# Revit family: Gira_239902
name_source: partatom
category: Electrical Fixtures
revit_build: Autodesk Revit 2017 (Build: 20160225_1515(x64)
units: mm (PartAtom-declared; Revit-internal decimal feet)

## family parameters
Cut with Voids When Loaded = No
Host = Face
Maintain Annotation Orientation = Yes
Part Type = Normal
Room Calculation Point = No
Round Connector Dimension = Use Diameter
Shared = No

## types (1)
- Pres. + motion detec. 360° Kompakt Sentinel
    Available = No
    BIM (1) = https://media.stage.bim.site
    Category = Accessories for movement sensor
    Data sheet (1) = https://katalog.gira.de
    Default Elevation = 1219 mm
    Description = Pres. mot.det.360° Kompakt Sent,Presence detector and motion detector 360 compact,,,Features:,- Automatic switching of lighting, depending on the movement of heat and ambient brightness.,- 2-point light control.,- Functions can be adjusted with IR remote controls.,- Restricting the detection field by switching off individual sensors or clip-on panel.,- Operation with IR remote control, auxiliary unit 2-wire or rocker button.,- Teach-in function for adapting the brightness threshold, in combination with IR remote controls.,- Switch-off pre-warning.,- Short-term operation, e.g. for controlling acoustic signal transmitters.,- Occupied-home simulation.,- Function as twilight switch.,- Dynamic delay time.,- Extension of the detection field by connecting several devices in parallel.,,Notes :,- The required settings for start-up are carried out with the IR remote control PIR 1 (accessory) for the installer.,- Ceiling mounting indoors, surface-mounted.
    GTIN = 4010337019381
    HAN = 239902
    HeinzeBIM = https://bimportal.heinze.de
    Manufacturer = Gira
    Manufacturer URL = https://www.gira.de
    Name = Pres. + motion detec. 360° Kompakt Sentinel
    URL = http://katalog.gira.de

## geometry (parser evidence)
native form markers: Sweep x2
no freeform markers — native parametric forms only
